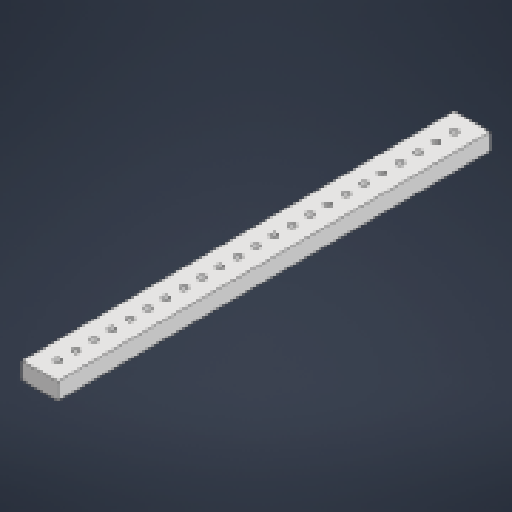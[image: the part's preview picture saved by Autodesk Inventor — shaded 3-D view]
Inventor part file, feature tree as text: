
AUTODESK INVENTOR PART (.ipt)
format: ipt  version: 2023 (Build 270158000, 158)  size: 156,160 bytes
history: native  units: in
note: dims shown in document units (in); Inventor stores cm internally (conversion verified against a paired STEP export)
features: sketch x2, extrude x1, hole x1
ambient origin geometry x8: Origin, YZ Plane, XZ Plane, XY Plane, X Axis, Y Axis, Z Axis, Center Point
bodies: Solid1 (feature_tree)
feature tree (4):
  extrude  "Extrusion1"  Depth=12.0in
  hole  "Hole1"  [1 undecoded]
  sketch  "Sketch1"  dims[d0=1.0in d1=12.0in]
  sketch  "Sketch2"  dims[d9=0.47in d10=0.0in d20=0.1875in d21=0.5in d22=9.0551in d24=0.5in d25=0.3937in d27=1.0in d29=0.1875in d30=0.75in d31=0.375in d32=0.25in d33=0.5635in d34=1.0in d35=0.8108in]
note: 1 required parameter value undecoded (feature->parameter linkage not recoverable at this tier; creation-order binding heuristic only, values carry confidence <= 0.55)
